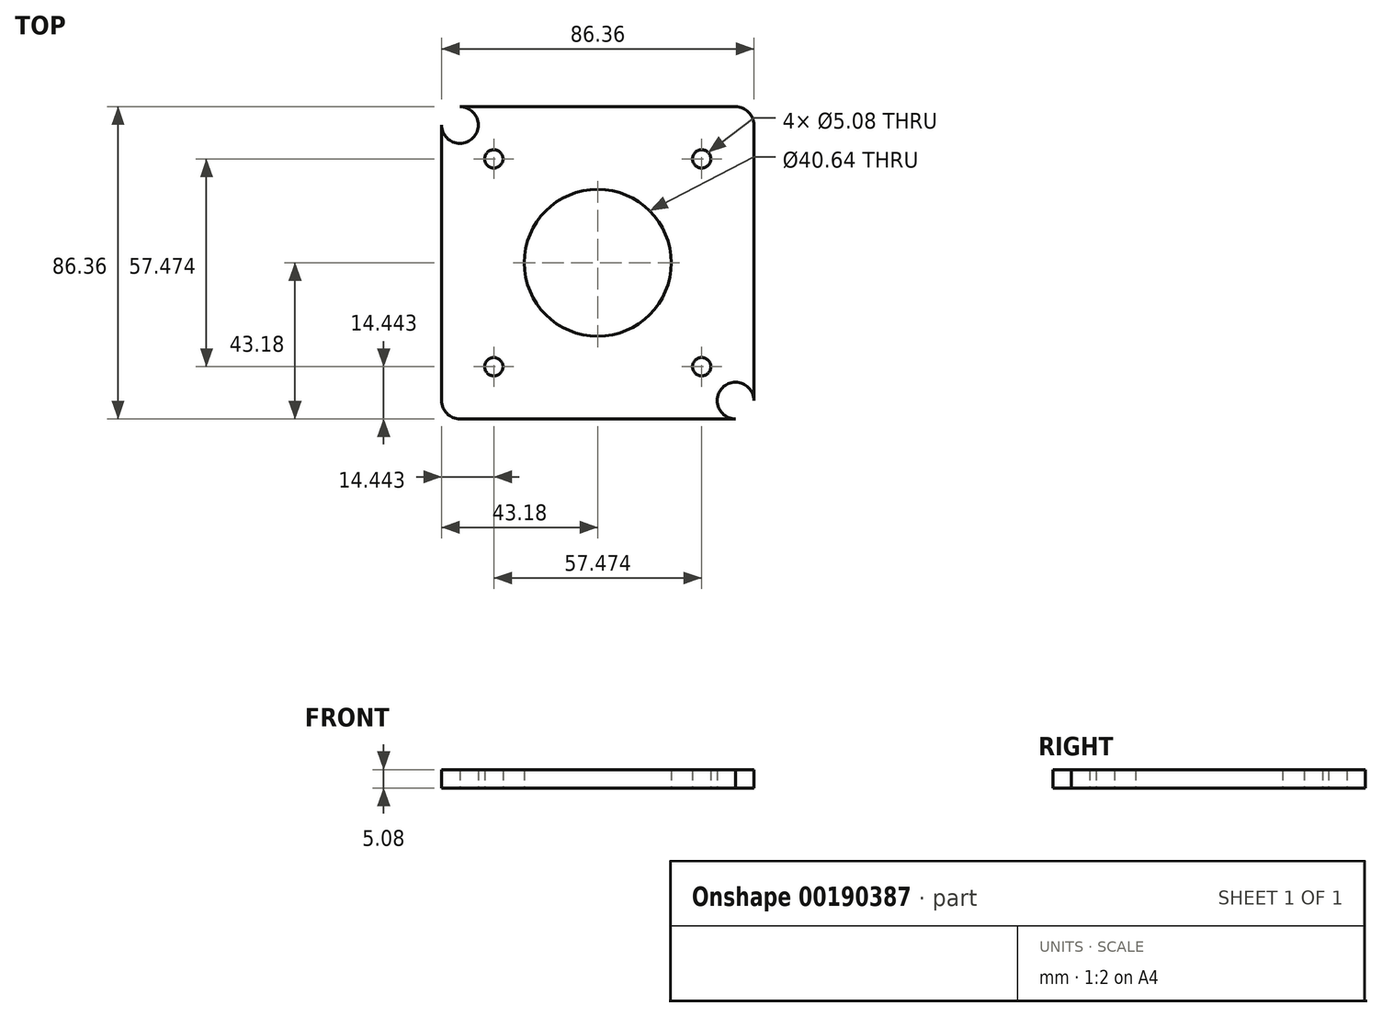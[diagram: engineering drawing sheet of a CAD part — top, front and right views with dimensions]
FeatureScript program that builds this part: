
annotation { "Feature Type Name" : "Feature", "Feature Type Description" : "" }
export const myFeature = defineFeature(function(context is Context, id is Id, definition is map)
    precondition{}
    {
        {
            var Q0;
            Q0=qCreatedBy(makeId("Top.planeOp"),FACE);
            var sketch = newSketch(context, id + "F0", { "sketchPlane" : qUnion([Q0])});
            skLineSegment(sketch, "E0.bottom", {"start": v(0, 0) * mm, "end": v(38.1, 0) * mm});
            skLineSegment(sketch, "E0.top", {"start": v(0, 38.1) * mm, "end": v(38.1, 38.1) * mm});
            skLineSegment(sketch, "E0.left", {"start": v(0, 0) * mm, "end": v(0, 38.1) * mm});
            skLineSegment(sketch, "E0.right", {"start": v(38.1, 0) * mm, "end": v(38.1, 38.1) * mm});
            skCircle(sketch, "E1", {"center": v(38.1, 38.1) * mm, "radius": 5.08 * mm});
            skLineSegment(sketch, "E2", {"start": v(38.1, 38.1) * mm, "end": v(41.7, 41.68) * mm});
            skLineSegment(sketch, "E3", {"start": v(38.1, 0) * mm, "end": v(43.18, 0) * mm});
            skLineSegment(sketch, "E4", {"start": v(0, 38.1) * mm, "end": v(0, 43.18) * mm});
            skLineSegment(sketch, "E5", {"start": v(0, 43.18) * mm, "end": v(38.1, 43.18) * mm});
            skLineSegment(sketch, "E6", {"start": v(43.18, 0) * mm, "end": v(43.18, 38.1) * mm});
            skLineSegment(sketch, "E7.MirrorCS", {"start": v(0, 43.18) * mm, "end": v(-38.1, 43.18) * mm});
            skCircle(sketch, "E8.MirrorC", {"center": v(-38.1, 38.1) * mm, "radius": 5.08 * mm});
            skLineSegment(sketch, "E9.MirrorCS", {"start": v(-43.18, 0) * mm, "end": v(-43.18, 38.1) * mm});
            skLineSegment(sketch, "E10.MirrorCS", {"start": v(0, -43.18) * mm, "end": v(38.1, -43.18) * mm});
            skCircle(sketch, "E11.MirrorC", {"center": v(38.1, -38.1) * mm, "radius": 5.08 * mm});
            skLineSegment(sketch, "E12.MirrorCS", {"start": v(43.18, 0) * mm, "end": v(43.18, -38.1) * mm});
            skLineSegment(sketch, "E13.MirrorCS", {"start": v(-43.18, 0) * mm, "end": v(-43.18, -38.1) * mm});
            skLineSegment(sketch, "E14.MirrorCS", {"start": v(0, -43.18) * mm, "end": v(-38.1, -43.18) * mm});
            skCircle(sketch, "E15.MirrorC", {"center": v(-38.1, -38.1) * mm, "radius": 5.08 * mm});
            skLineSegment(sketch, "E16", {"start": v(0, 0) * mm, "end": v(38.1, 38.1) * mm});
            skPoint(sketch, "E17", {"position": v(28.74, 28.74) * mm});
            skLineSegment(sketch, "E18", {"start": v(28.74, 28.74) * mm, "end": v(0, 0) * mm});
            skCircle(sketch, "E19", {"center": v(28.74, 28.74) * mm, "radius": 2.54 * mm});
            skLineSegment(sketch, "E20", {"start": v(28.74, 28.74) * mm, "end": v(26.52, 29.98) * mm});
            skCircle(sketch, "E21.MirrorC", {"center": v(-28.74, 28.74) * mm, "radius": 2.54 * mm});
            skCircle(sketch, "E22.MirrorC", {"center": v(-28.74, -28.74) * mm, "radius": 2.54 * mm});
            skCircle(sketch, "E23.MirrorC", {"center": v(28.74, -28.74) * mm, "radius": 2.54 * mm});
            skCircle(sketch, "E24", {"center": v(0, 0) * mm, "radius": 20.32 * mm});
            skLineSegment(sketch, "E25", {"start": v(0, 0) * mm, "end": v(-13.59, -15.11) * mm});
            skSolve(sketch);
        }
        {
            var Q0;
            {var subQ0=sQuery(id+"F0.wireOp",EDGE,"E8.MirrorC");var subQ1=makeQuery(id+"F0.imprint","INTERSECT",VERTEX,{"derivedFrom":[sQuery(id+"F0.wireOp",EDGE,"E7.MirrorCS"),subQ0]});Q0=makeQuery(id+"F0.imprint","IMPRINT",FACE,{"disambiguationData":[TD([[makeQuery(id+"F0.imprint","IMPRINT",EDGE,{"disambiguationData":[TD([[subQ1,1.0]])],"derivedFrom":subQ0}),-1.0]])]});}
            var Q1;
            {var subQ0=sQuery(id+"F0.wireOp",EDGE,"E15.MirrorC");var subQ1=makeQuery(id+"F0.imprint","INTERSECT",VERTEX,{"derivedFrom":[sQuery(id+"F0.wireOp",EDGE,"E13.MirrorCS"),subQ0]});Q1=makeQuery(id+"F0.imprint","IMPRINT",FACE,{"disambiguationData":[TD([[makeQuery(id+"F0.imprint","IMPRINT",EDGE,{"disambiguationData":[TD([[subQ1,-1.0]])],"derivedFrom":subQ0}),1.0]])]});}
            var Q2;
            {var subQ0=sQuery(id+"F0.wireOp",EDGE,"E4");Q2=makeQuery(id+"F0.imprint","IMPRINT",FACE,{"disambiguationData":[TD([[makeQuery(id+"F0.imprint","IMPRINT",EDGE,{"derivedFrom":subQ0}),-1.0]])]});}
            var Q3;
            {var subQ0=sQuery(id+"F0.wireOp",EDGE,"E3");Q3=makeQuery(id+"F0.imprint","IMPRINT",FACE,{"disambiguationData":[TD([[makeQuery(id+"F0.imprint","IMPRINT",EDGE,{"derivedFrom":subQ0}),1.0]])]});}
            var Q4;
            {var subQ0=sQuery(id+"F0.wireOp",EDGE,"E2");Q4=makeQuery(id+"F0.imprint","IMPRINT",FACE,{"disambiguationData":[TD([[makeQuery(id+"F0.imprint","IMPRINT",EDGE,{"derivedFrom":subQ0}),-1.0]])]});}
            var Q5;
            {var subQ0=sQuery(id+"F0.wireOp",EDGE,"E2");Q5=makeQuery(id+"F0.imprint","IMPRINT",FACE,{"disambiguationData":[TD([[makeQuery(id+"F0.imprint","IMPRINT",EDGE,{"derivedFrom":subQ0}),1.0]])]});}
            var Q6;
            {var subQ1=sQuery(id+"F0.wireOp",EDGE,"E0.top");var subQ3=sQuery(id+"F0.wireOp",EDGE,"E1");var subQ4=makeQuery(id+"F0.imprint","INTERSECT",VERTEX,{"derivedFrom":[subQ1,subQ3]});Q6=makeQuery(id+"F0.imprint","IMPRINT",FACE,{"disambiguationData":[TD([[makeQuery(id+"F0.imprint","IMPRINT",EDGE,{"disambiguationData":[TD([[subQ4,-1.0]])],"derivedFrom":subQ3}),1.0]])]});}
            var Q7;
            {var subQ1=sQuery(id+"F0.wireOp",EDGE,"E0.right");var subQ3=sQuery(id+"F0.wireOp",EDGE,"E1");var subQ4=makeQuery(id+"F0.imprint","INTERSECT",VERTEX,{"derivedFrom":[subQ1,subQ3]});Q7=makeQuery(id+"F0.imprint","IMPRINT",FACE,{"disambiguationData":[TD([[makeQuery(id+"F0.imprint","IMPRINT",EDGE,{"disambiguationData":[TD([[subQ4,1.0]])],"derivedFrom":subQ3}),1.0]])]});}
            var Q8;
            {var subQ0=sQuery(id+"F0.wireOp",EDGE,"E11.MirrorC");var subQ1=makeQuery(id+"F0.imprint","INTERSECT",VERTEX,{"derivedFrom":[sQuery(id+"F0.wireOp",EDGE,"E10.MirrorCS"),subQ0]});Q8=makeQuery(id+"F0.imprint","IMPRINT",FACE,{"disambiguationData":[TD([[makeQuery(id+"F0.imprint","IMPRINT",EDGE,{"disambiguationData":[TD([[subQ1,1.0]])],"derivedFrom":subQ0}),-1.0]])]});}
            var Q9;
            {var subQ4=sQuery(id+"F0.wireOp",EDGE,"E3");Q9=makeQuery(id+"F0.imprint","IMPRINT",FACE,{"disambiguationData":[TD([[makeQuery(id+"F0.imprint","IMPRINT",EDGE,{"derivedFrom":subQ4}),-1.0]])]});}
            var Q10;
            {var subQ0=sQuery(id+"F0.wireOp",EDGE,"E1");var subQ1=sQuery(id+"F0.wireOp",EDGE,"E0.right");var subQ2=makeQuery(id+"F0.imprint","INTERSECT",VERTEX,{"derivedFrom":[subQ1,subQ0]});Q10=makeQuery(id+"F0.imprint","IMPRINT",FACE,{"disambiguationData":[TD([[makeQuery(id+"F0.imprint","IMPRINT",EDGE,{"disambiguationData":[TD([[subQ2,1.0]])],"derivedFrom":subQ0}),-1.0]])]});}
            var Q11;
            {var subQ0=sQuery(id+"F0.wireOp",EDGE,"E1");var subQ1=sQuery(id+"F0.wireOp",EDGE,"E0.top");var subQ2=makeQuery(id+"F0.imprint","INTERSECT",VERTEX,{"derivedFrom":[subQ1,subQ0]});Q11=makeQuery(id+"F0.imprint","IMPRINT",FACE,{"disambiguationData":[TD([[makeQuery(id+"F0.imprint","IMPRINT",EDGE,{"disambiguationData":[TD([[subQ2,-1.0]])],"derivedFrom":subQ0}),-1.0]])]});}
            extrude(context, id + "F1", {"entities" : qUnion([Q0, Q1, Q2, Q3, Q4, Q5, Q6, Q7, Q8, Q9, Q10, Q11]), "depth" : 5.08 * mm});
        }
    });
